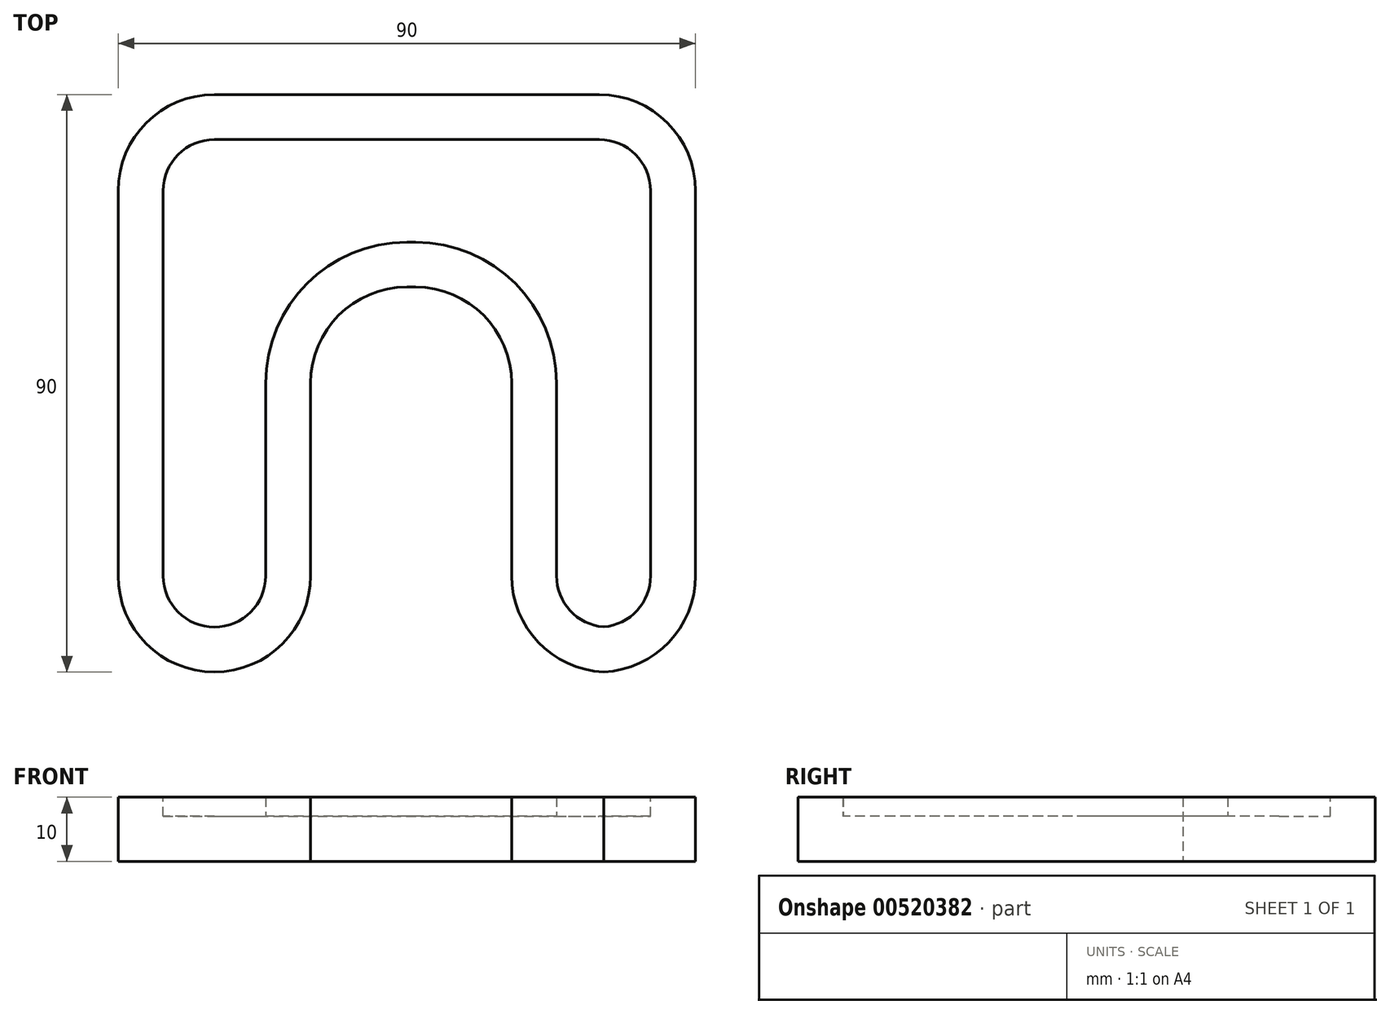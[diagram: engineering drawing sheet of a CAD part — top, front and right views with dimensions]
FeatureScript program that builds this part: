
annotation { "Feature Type Name" : "Feature", "Feature Type Description" : "" }
export const myFeature = defineFeature(function(context is Context, id is Id, definition is map)
    precondition{}
    {
        {
            var Q0;
            Q0=qCreatedBy(makeId("Top.planeOp"),FACE);
            var sketch = newSketch(context, id + "F0", { "sketchPlane" : qUnion([Q0])});
            skLineSegment(sketch, "E0", {"start": v(-85.82, -11.08) * mm, "end": v(-85.82, 48.92) * mm});
            skLineSegment(sketch, "E1", {"start": v(-70.82, 63.92) * mm, "end": v(-10.82, 63.92) * mm});
            skLineSegment(sketch, "E2", {"start": v(4.18, 48.92) * mm, "end": v(4.18, -11.08) * mm});
            skLineSegment(sketch, "E3", {"start": v(-9.48, -26.08) * mm, "end": v(-10.82, -26.08) * mm});
            skLineSegment(sketch, "E4", {"start": v(-24.48, -11.08) * mm, "end": v(-24.48, 18.92) * mm});
            skLineSegment(sketch, "E5", {"start": v(-39.48, 33.92) * mm, "end": v(-40.82, 33.92) * mm});
            skLineSegment(sketch, "E6", {"start": v(-55.82, 18.92) * mm, "end": v(-55.82, -11.08) * mm});
            skLineSegment(sketch, "E7", {"start": v(-70.82, -26.08) * mm, "end": v(-70.82, -26.08) * mm});
            skPoint(sketch, "E8.visualSharp", {"position": v(-85.82, 63.92) * mm});
            skArc(sketch, "E8.filletArc", {"start": v(-70.82, 63.92) * mm, "mid": v(-81.43, 59.52) * mm, "end": v(-85.82, 48.92) * mm});
            skPoint(sketch, "E9.visualSharp", {"position": v(4.18, 63.92) * mm});
            skArc(sketch, "E9.filletArc", {"start": v(4.18, 48.92) * mm, "mid": v(-0.21, 59.52) * mm, "end": v(-10.82, 63.92) * mm});
            skPoint(sketch, "E10.visualSharp", {"position": v(4.18, -26.08) * mm});
            skArc(sketch, "E10.filletArc", {"start": v(-10.82, -26.08) * mm, "mid": v(-0.21, -21.69) * mm, "end": v(4.18, -11.08) * mm});
            skPoint(sketch, "E11.visualSharp", {"position": v(-24.48, -26.08) * mm});
            skArc(sketch, "E11.filletArc", {"start": v(-24.48, -11.08) * mm, "mid": v(-20.09, -21.69) * mm, "end": v(-9.48, -26.08) * mm});
            skPoint(sketch, "E12.visualSharp", {"position": v(-24.48, 33.92) * mm});
            skArc(sketch, "E12.filletArc", {"start": v(-24.48, 18.92) * mm, "mid": v(-28.88, 29.52) * mm, "end": v(-39.48, 33.92) * mm});
            skPoint(sketch, "E13.visualSharp", {"position": v(-55.82, 33.92) * mm});
            skArc(sketch, "E13.filletArc", {"start": v(-40.82, 33.92) * mm, "mid": v(-51.43, 29.52) * mm, "end": v(-55.82, 18.92) * mm});
            skPoint(sketch, "E14.visualSharp", {"position": v(-55.82, -26.08) * mm});
            skArc(sketch, "E14.filletArc", {"start": v(-70.82, -26.08) * mm, "mid": v(-60.21, -21.69) * mm, "end": v(-55.82, -11.08) * mm});
            skPoint(sketch, "E15.visualSharp", {"position": v(-85.82, -26.08) * mm});
            skArc(sketch, "E15.filletArc", {"start": v(-85.82, -11.08) * mm, "mid": v(-81.43, -21.69) * mm, "end": v(-70.82, -26.08) * mm});
            skSolve(sketch);
        }
        {
            var Q0;
            Q0=makeQuery(id+"F0.imprint","IMPRINT",FACE,{"disambiguationData":[TD([[makeQuery(id+"F0.imprint","IMPRINT",EDGE,{"derivedFrom":sQuery(id+"F0.wireOp",EDGE,"E0")}),-1.0]])]});
            extrude(context, id + "F1", {"entities" : qUnion([Q0]), "depth" : 10 * mm, "offsetDistance" : 25 * mm});
        }
        {
            var Q0;
            Q0=makeQuery(id+"F1.opExtrude","CAP_FACE",FACE,{"disambiguationData":[OSD([sQuery(id+"F0.wireOp",EDGE,"E0"),sQuery(id+"F0.wireOp",EDGE,"E1"),sQuery(id+"F0.wireOp",EDGE,"E2"),sQuery(id+"F0.wireOp",EDGE,"E4"),sQuery(id+"F0.wireOp",EDGE,"E5"),sQuery(id+"F0.wireOp",EDGE,"E6"),sQuery(id+"F0.wireOp",EDGE,"E8.filletArc"),sQuery(id+"F0.wireOp",EDGE,"E9.filletArc"),sQuery(id+"F0.wireOp",EDGE,"E10.filletArc"),sQuery(id+"F0.wireOp",EDGE,"E11.filletArc"),sQuery(id+"F0.wireOp",EDGE,"E12.filletArc"),sQuery(id+"F0.wireOp",EDGE,"E13.filletArc"),sQuery(id+"F0.wireOp",EDGE,"E14.filletArc"),sQuery(id+"F0.wireOp",EDGE,"E15.filletArc")])],"isStart":false});
            shell(context, id + "F2", {"entities" : qUnion([Q0]), "thickness" : 7 * mm});
        }
    });
